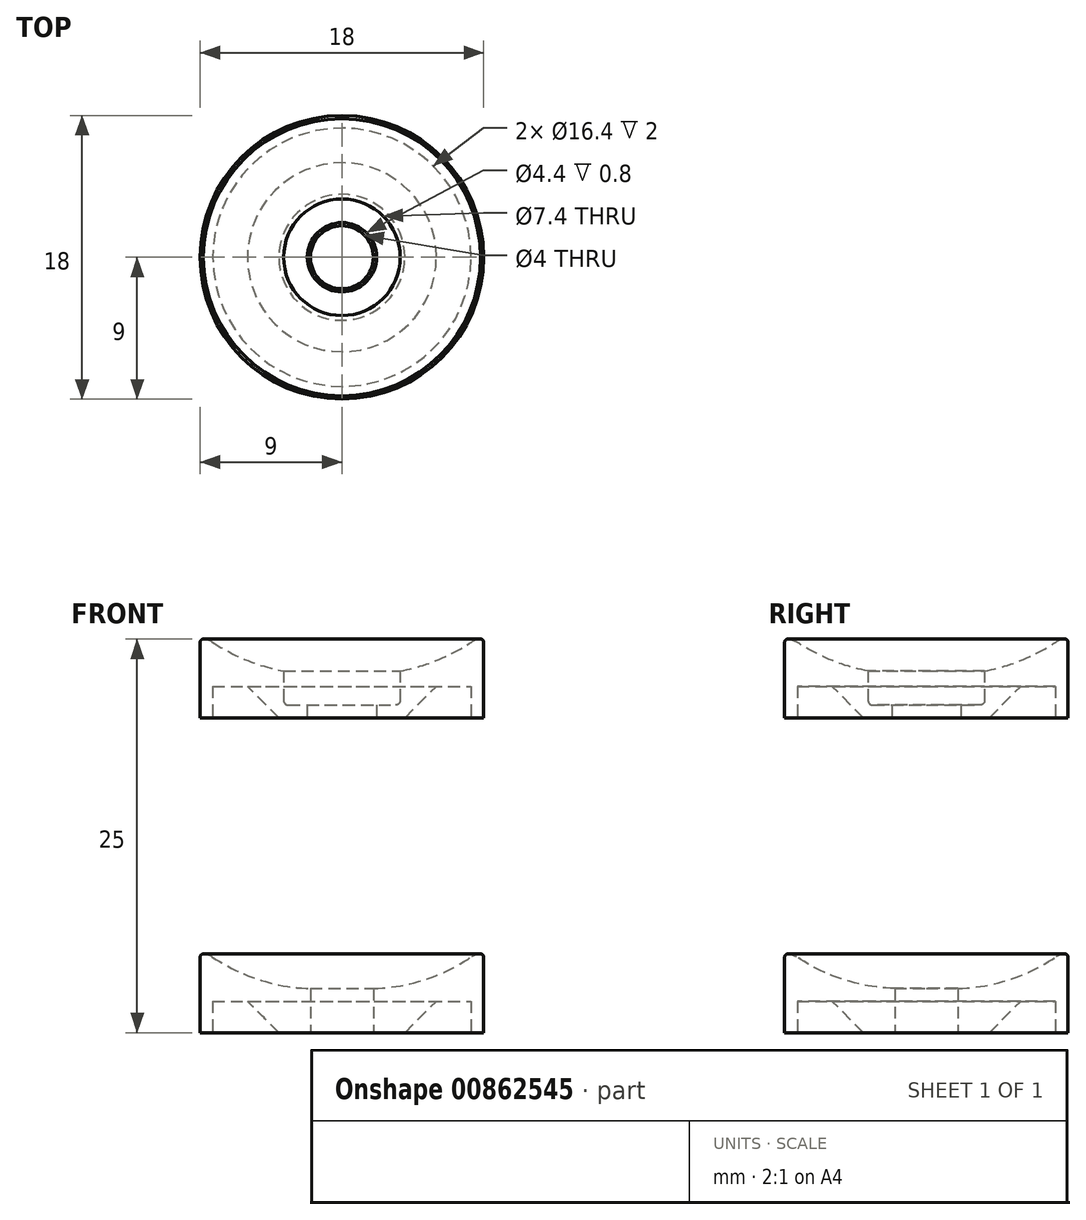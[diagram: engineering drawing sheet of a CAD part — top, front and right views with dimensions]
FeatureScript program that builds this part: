
annotation { "Feature Type Name" : "Feature", "Feature Type Description" : "" }
export const myFeature = defineFeature(function(context is Context, id is Id, definition is map)
    precondition{}
    {
        {
            var Q0;
            Q0=qCreatedBy(makeId("Front.planeOp"),FACE);
            var sketch = newSketch(context, id + "F0", { "sketchPlane" : qUnion([Q0])});
            skLineSegment(sketch, "E0", {"start": v(-2, 2.8) * mm, "end": v(-2, 0) * mm});
            skLineSegment(sketch, "E1", {"start": v(-2, 0) * mm, "end": v(-9, 0) * mm});
            skLineSegment(sketch, "E2", {"start": v(-9, 0) * mm, "end": v(-9, 4.8) * mm});
            skLineSegment(sketch, "E3", {"start": v(-8.81, 5) * mm, "end": v(-8.8, 5) * mm});
            skArc(sketch, "E4", {"start": v(-8.25, 4.83) * mm, "mid": v(-5.27, 3.37) * mm, "end": v(-2, 2.8) * mm});
            skLineSegment(sketch, "E5", {"start": v(0, 0) * mm, "end": v(0, 2.27) * mm});
            skLineSegment(sketch, "E6", {"start": v(-2, 0.8) * mm, "end": v(-3.4, 0.8) * mm});
            skLineSegment(sketch, "E7", {"start": v(-3.7, 1.1) * mm, "end": v(-3.7, 2.98) * mm});
            skPoint(sketch, "E8.visualSharp", {"position": v(-8.5, 5) * mm});
            skArc(sketch, "E8.filletArc", {"start": v(-8.25, 4.83) * mm, "mid": v(-8.52, 4.96) * mm, "end": v(-8.81, 5) * mm});
            skPoint(sketch, "E9.visualSharp", {"position": v(-9, 5) * mm});
            skArc(sketch, "E9.filletArc", {"start": v(-8.8, 5) * mm, "mid": v(-8.94, 4.94) * mm, "end": v(-9, 4.8) * mm});
            skLineSegment(sketch, "E10", {"start": v(-6, 2) * mm, "end": v(-4, 0) * mm});
            skLineSegment(sketch, "E11", {"start": v(-2.2, 0.8) * mm, "end": v(-2.2, 0) * mm});
            skPoint(sketch, "E12.visualSharp", {"position": v(-3.7, 0.8) * mm});
            skArc(sketch, "E12.filletArc", {"start": v(-3.7, 1.1) * mm, "mid": v(-3.61, 0.89) * mm, "end": v(-3.4, 0.8) * mm});
            skLineSegment(sketch, "E13", {"start": v(-6, 2) * mm, "end": v(-8.2, 2) * mm});
            skLineSegment(sketch, "E14", {"start": v(-8.2, 2) * mm, "end": v(-8.2, 0) * mm});
            skSolve(sketch);
        }
        {
            var Q0;
            {var subQ0=sQuery(id+"F0.wireOp",EDGE,"E7");Q0=makeQuery(id+"F0.imprint","IMPRINT",FACE,{"disambiguationData":[TD([[makeQuery(id+"F0.imprint","IMPRINT",EDGE,{"derivedFrom":subQ0}),1.0]])]});}
            var Q1;
            {var subQ5=sQuery(id+"F0.wireOp",EDGE,"E11");Q1=makeQuery(id+"F0.imprint","IMPRINT",FACE,{"disambiguationData":[TD([[makeQuery(id+"F0.imprint","IMPRINT",EDGE,{"derivedFrom":subQ5}),1.0]])]});}
            var Q2;
            {var subQ0=sQuery(id+"F0.wireOp",EDGE,"E7");Q2=makeQuery(id+"F0.imprint","IMPRINT",FACE,{"disambiguationData":[TD([[makeQuery(id+"F0.imprint","IMPRINT",EDGE,{"derivedFrom":subQ0}),-1.0]])]});}
            var Q3;
            Q3=sQuery(id+"F0.wireOp",EDGE,"E5");
            revolve(context, id + "F1", {"surfaceOperationType" : NewSurfaceOperationType.NEW, "entities" : qUnion([Q0, Q1, Q2]), "axis" : qUnion([Q3]), "revolveType" : RevolveType.FULL});
        }
        {
            var Q0;
            Q0=makeQuery(id+"F1.opRevolve","SWEPT_BODY",BODY,{"disambiguationData":[OSD([sQuery(id+"F0.wireOp",EDGE,"E0"),sQuery(id+"F0.wireOp",EDGE,"E1"),sQuery(id+"F0.wireOp",EDGE,"E2"),sQuery(id+"F0.wireOp",EDGE,"E3"),sQuery(id+"F0.wireOp",EDGE,"E4")])]});
            transform(context, id + "F2", {"entities" : qUnion([Q0]), "transformType" : TransformType.TRANSLATION_3D, "dx" : 0 * mm, "dy" : 0 * mm, "dz" : -20 * mm, "makeCopy" : false});
        }
        {
            var Q0;
            {var subQ0=sQuery(id+"F0.wireOp",EDGE,"E7");Q0=makeQuery(id+"F0.imprint","IMPRINT",FACE,{"disambiguationData":[TD([[makeQuery(id+"F0.imprint","IMPRINT",EDGE,{"derivedFrom":subQ0}),1.0]])]});}
            var Q1;
            Q1=sQuery(id+"F0.wireOp",EDGE,"E5");
            revolve(context, id + "F3", {"surfaceOperationType" : NewSurfaceOperationType.NEW, "entities" : qUnion([Q0]), "axis" : qUnion([Q1]), "revolveType" : RevolveType.FULL});
        }
    });
